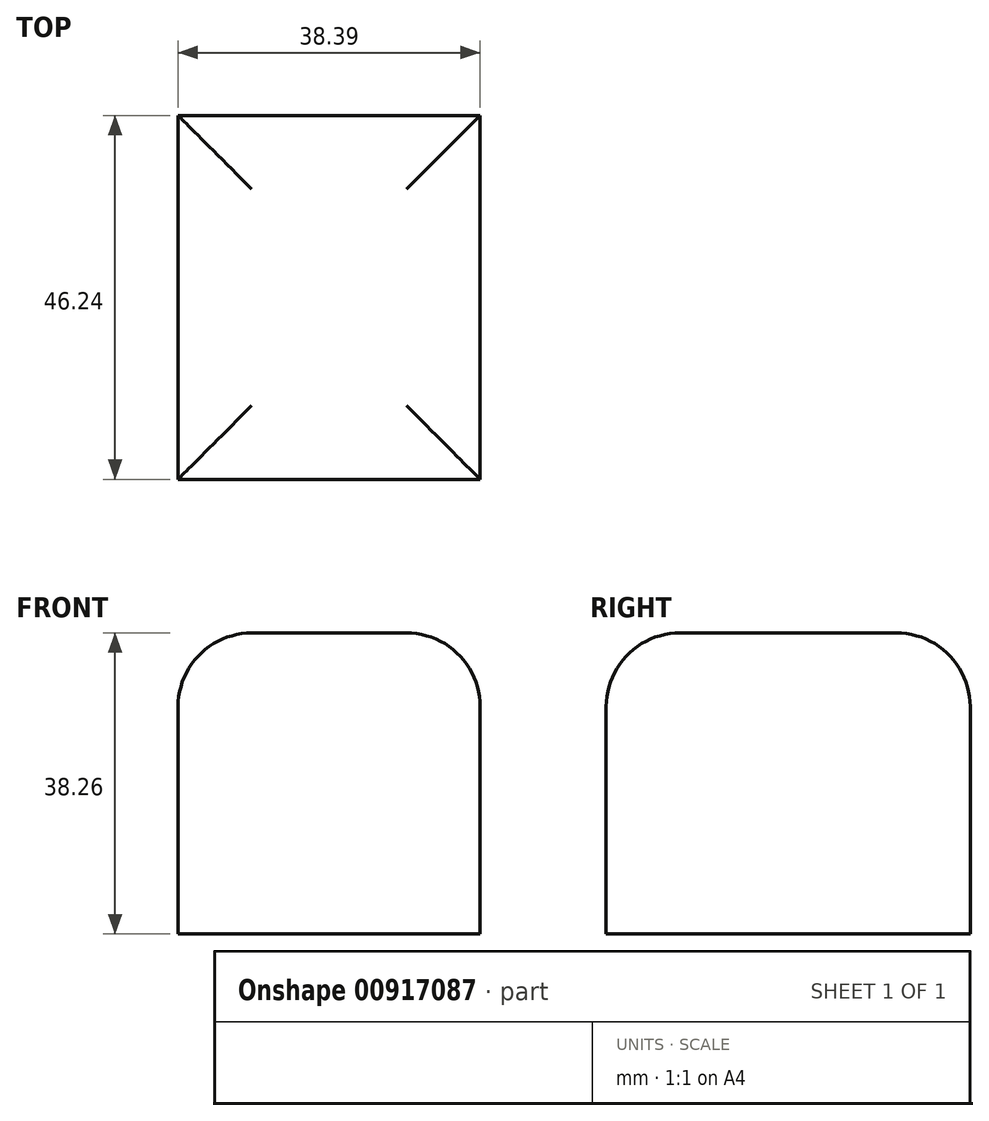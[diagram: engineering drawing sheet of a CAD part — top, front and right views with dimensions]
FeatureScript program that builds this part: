
annotation { "Feature Type Name" : "Feature", "Feature Type Description" : "" }
export const myFeature = defineFeature(function(context is Context, id is Id, definition is map)
    precondition{}
    {
        {
            var Q0;
            Q0=qCreatedBy(makeId("Top.planeOp"),FACE);
            var sketch = newSketch(context, id + "F0", { "sketchPlane" : qUnion([Q0])});
            skLineSegment(sketch, "E0.bottom", {"start": v(0, 0) * mm, "end": v(38.39, 0) * mm});
            skLineSegment(sketch, "E0.top", {"start": v(0, -46.24) * mm, "end": v(38.39, -46.24) * mm});
            skLineSegment(sketch, "E0.left", {"start": v(0, 0) * mm, "end": v(0, -46.24) * mm});
            skLineSegment(sketch, "E0.right", {"start": v(38.39, 0) * mm, "end": v(38.39, -46.24) * mm});
            skSolve(sketch);
        }
        {
            var Q0;
            Q0=makeQuery(id+"F0.imprint","IMPRINT",FACE,{"disambiguationData":[TD([[makeQuery(id+"F0.imprint","IMPRINT",EDGE,{"derivedFrom":sQuery(id+"F0.wireOp",EDGE,"E0.bottom")}),-1.0]])]});
            extrude(context, id + "F1", {"entities" : qUnion([Q0]), "depth" : 38.26 * mm, "offsetDistance" : 25 * mm});
        }
        {
            var Q0;
            Q0=makeQuery(id+"F1.opExtrude","CAP_EDGE",EDGE,{"disambiguationData":[OSD([sQuery(id+"F0.wireOp",EDGE,"E0.bottom")])],"isStart":false});
            var Q1;
            Q1=makeQuery(id+"F1.opExtrude","CAP_EDGE",EDGE,{"disambiguationData":[OSD([sQuery(id+"F0.wireOp",EDGE,"E0.top")])],"isStart":false});
            var Q2;
            Q2=makeQuery(id+"F1.opExtrude","CAP_EDGE",EDGE,{"disambiguationData":[OSD([sQuery(id+"F0.wireOp",EDGE,"E0.left")])],"isStart":false});
            var Q3;
            Q3=makeQuery(id+"F1.opExtrude","CAP_EDGE",EDGE,{"disambiguationData":[OSD([sQuery(id+"F0.wireOp",EDGE,"E0.right")])],"isStart":false});
            fillet(context, id + "F2", {"entities" : qUnion([Q0, Q1, Q2, Q3]), "radius" : 9.36 * mm, "tangentPropagation" : true, "allowEdgeOverflow" : false});
        }
    });
